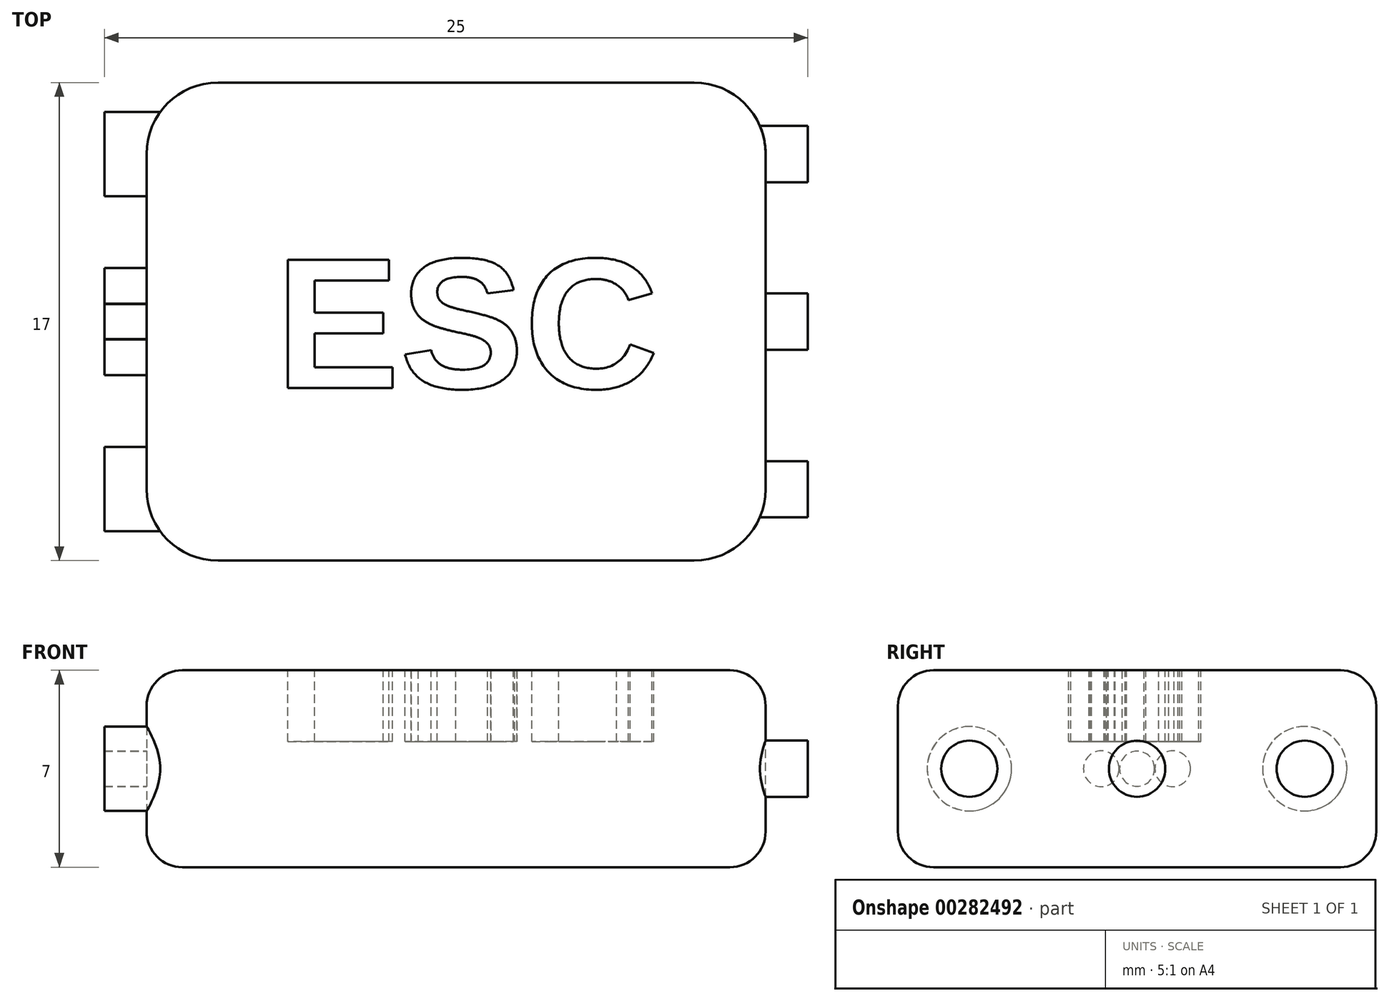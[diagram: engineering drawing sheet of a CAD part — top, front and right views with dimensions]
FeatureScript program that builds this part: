
annotation { "Feature Type Name" : "Feature", "Feature Type Description" : "" }
export const myFeature = defineFeature(function(context is Context, id is Id, definition is map)
    precondition{}
    {
        {
            var Q0;
            Q0=qCreatedBy(makeId("Top.planeOp"),FACE);
            var sketch = newSketch(context, id + "F0", { "sketchPlane" : qUnion([Q0])});
            skLineSegment(sketch, "E0.bottom", {"start": v(0, 0) * mm, "end": v(22, 0) * mm});
            skLineSegment(sketch, "E0.top", {"start": v(0, 17) * mm, "end": v(22, 17) * mm});
            skLineSegment(sketch, "E0.left", {"start": v(0, 0) * mm, "end": v(0, 17) * mm});
            skLineSegment(sketch, "E0.right", {"start": v(22, 0) * mm, "end": v(22, 17) * mm});
            skSolve(sketch);
        }
        {
            var Q0;
            Q0=makeQuery(id+"F0.imprint","IMPRINT",FACE,{"disambiguationData":[TD([[makeQuery(id+"F0.imprint","IMPRINT",EDGE,{"derivedFrom":sQuery(id+"F0.wireOp",EDGE,"E0.bottom")}),1.0]])]});
            extrude(context, id + "F1", {"entities" : qUnion([Q0]), "depth" : 7 * mm});
        }
        {
            var Q0;
            Q0=makeQuery(id+"F1.opExtrude","SWEPT_EDGE",EDGE,{"disambiguationData":[OSD([sQuery(id+"F0.wireOp",EDGE,"E0.bottom"),sQuery(id+"F0.wireOp",EDGE,"E0.left")])]});
            var Q1;
            Q1=makeQuery(id+"F1.opExtrude","SWEPT_EDGE",EDGE,{"disambiguationData":[OSD([sQuery(id+"F0.wireOp",EDGE,"E0.top"),sQuery(id+"F0.wireOp",EDGE,"E0.right")])]});
            var Q2;
            Q2=makeQuery(id+"F1.opExtrude","SWEPT_EDGE",EDGE,{"disambiguationData":[OSD([sQuery(id+"F0.wireOp",EDGE,"E0.bottom"),sQuery(id+"F0.wireOp",EDGE,"E0.right")])]});
            var Q3;
            Q3=makeQuery(id+"F1.opExtrude","SWEPT_EDGE",EDGE,{"disambiguationData":[OSD([sQuery(id+"F0.wireOp",EDGE,"E0.top"),sQuery(id+"F0.wireOp",EDGE,"E0.left")])]});
            fillet(context, id + "F2", {"entities" : qUnion([Q0, Q1, Q2, Q3]), "radius" : 2.54 * mm, "tangentPropagation" : true, "allowEdgeOverflow" : false});
        }
        {
            var Q0;
            Q0=makeQuery(id+"F1.opExtrude","CAP_EDGE",EDGE,{"disambiguationData":[OSD([sQuery(id+"F0.wireOp",EDGE,"E0.top")])],"isStart":false});
            fillet(context, id + "F3", {"entities" : qUnion([Q0]), "radius" : 1.27 * mm, "tangentPropagation" : true, "allowEdgeOverflow" : false});
        }
        {
            var Q0;
            Q0=makeQuery(id+"F1.opExtrude","CAP_FACE",FACE,{"disambiguationData":[OSD([sQuery(id+"F0.wireOp",EDGE,"E0.bottom"),sQuery(id+"F0.wireOp",EDGE,"E0.top"),sQuery(id+"F0.wireOp",EDGE,"E0.left"),sQuery(id+"F0.wireOp",EDGE,"E0.right")])],"isStart":false});
            var sketch = newSketch(context, id + "F4", { "sketchPlane" : qUnion([Q0])});
            skText(sketch, "E1", { "text": "ESC", "fontName": "Arimo-Bold.ttf"});
            const initialGuessF4  = {"E1": [0.00458, 0.00614, 1, 0, 0.00477]};
            skSetInitialGuess(sketch, initialGuessF4);
            skSolve(sketch);
        }
        {
            var Q0;
            Q0 = qSketchRegion(id + "F4", true);
            extrude(context, id + "F5", {"entities" : qUnion([Q0]), "operationType" : NewBodyOperationType.REMOVE, "oppositeDirection" : true, "depth" : 2.54 * mm});
        }
        {
            var Q0;
            Q0=makeQuery(id+"F1.opExtrude","SWEPT_FACE",FACE,{"disambiguationData":[OSD([sQuery(id+"F0.wireOp",EDGE,"E0.left")])]});
            var sketch = newSketch(context, id + "F6", { "sketchPlane" : qUnion([Q0])});
            skCircle(sketch, "E2", {"center": v(-2.54, 3.5) * mm, "radius": 1.5 * mm});
            skCircle(sketch, "E3", {"center": v(-14.46, 3.5) * mm, "radius": 1.5 * mm});
            skSolve(sketch);
        }
        {
            var Q0;
            {var subQ0=sQuery(id+"F6.wireOp",EDGE,"E3");var subQ1=sQuery(id+"F0.wireOp",EDGE,"E0.left");var subQ2=makeQuery(id+"F2.opFillet","BLEND_EDGE",EDGE,{"blendedFrom":[makeQuery(id+"F1.opExtrude","SWEPT_EDGE",EDGE,{"disambiguationData":[OSD([sQuery(id+"F0.wireOp",EDGE,"E0.top"),subQ1])]}),makeQuery(id+"F1.opExtrude","SWEPT_FACE",FACE,{"disambiguationData":[OSD([subQ1])]})],"blendedInto":[makeQuery(id+"F1.opExtrude","SWEPT_FACE",FACE,{"disambiguationData":[OSD([subQ1])]})]});var subQ3=makeQuery(id+"F6.imprint","INTERSECT",VERTEX,{"disambiguationData":[OD(0.0)],"derivedFrom":[subQ2,subQ0]});Q0=makeQuery(id+"F6.imprint","IMPRINT",FACE,{"disambiguationData":[TD([[makeQuery(id+"F6.imprint","IMPRINT",EDGE,{"disambiguationData":[TD([[subQ3,-1.0]])],"derivedFrom":subQ0}),1.0]])]});}
            var Q1;
            {var subQ0=sQuery(id+"F6.wireOp",EDGE,"E3");var subQ1=sQuery(id+"F0.wireOp",EDGE,"E0.left");var subQ2=makeQuery(id+"F2.opFillet","BLEND_EDGE",EDGE,{"blendedFrom":[makeQuery(id+"F1.opExtrude","SWEPT_EDGE",EDGE,{"disambiguationData":[OSD([sQuery(id+"F0.wireOp",EDGE,"E0.top"),subQ1])]}),makeQuery(id+"F1.opExtrude","SWEPT_FACE",FACE,{"disambiguationData":[OSD([subQ1])]})],"blendedInto":[makeQuery(id+"F1.opExtrude","SWEPT_FACE",FACE,{"disambiguationData":[OSD([subQ1])]})]});var subQ3=makeQuery(id+"F6.imprint","INTERSECT",VERTEX,{"disambiguationData":[OD(0.0)],"derivedFrom":[subQ2,subQ0]});Q1=makeQuery(id+"F6.imprint","IMPRINT",FACE,{"disambiguationData":[TD([[makeQuery(id+"F6.imprint","IMPRINT",EDGE,{"disambiguationData":[TD([[subQ3,1.0]])],"derivedFrom":subQ0}),1.0]])]});}
            var Q2;
            {var subQ0=sQuery(id+"F6.wireOp",EDGE,"E2");var subQ1=sQuery(id+"F0.wireOp",EDGE,"E0.left");var subQ2=makeQuery(id+"F2.opFillet","BLEND_EDGE",EDGE,{"blendedFrom":[makeQuery(id+"F1.opExtrude","SWEPT_EDGE",EDGE,{"disambiguationData":[OSD([sQuery(id+"F0.wireOp",EDGE,"E0.bottom"),subQ1])]}),makeQuery(id+"F1.opExtrude","SWEPT_FACE",FACE,{"disambiguationData":[OSD([subQ1])]})],"blendedInto":[makeQuery(id+"F1.opExtrude","SWEPT_FACE",FACE,{"disambiguationData":[OSD([subQ1])]})]});var subQ3=makeQuery(id+"F6.imprint","INTERSECT",VERTEX,{"disambiguationData":[OD(0.0)],"derivedFrom":[subQ2,subQ0]});Q2=makeQuery(id+"F6.imprint","IMPRINT",FACE,{"disambiguationData":[TD([[makeQuery(id+"F6.imprint","IMPRINT",EDGE,{"disambiguationData":[TD([[subQ3,-1.0]])],"derivedFrom":subQ0}),1.0]])]});}
            var Q3;
            {var subQ0=sQuery(id+"F6.wireOp",EDGE,"E2");var subQ1=sQuery(id+"F0.wireOp",EDGE,"E0.left");var subQ2=makeQuery(id+"F2.opFillet","BLEND_EDGE",EDGE,{"blendedFrom":[makeQuery(id+"F1.opExtrude","SWEPT_EDGE",EDGE,{"disambiguationData":[OSD([sQuery(id+"F0.wireOp",EDGE,"E0.bottom"),subQ1])]}),makeQuery(id+"F1.opExtrude","SWEPT_FACE",FACE,{"disambiguationData":[OSD([subQ1])]})],"blendedInto":[makeQuery(id+"F1.opExtrude","SWEPT_FACE",FACE,{"disambiguationData":[OSD([subQ1])]})]});var subQ3=makeQuery(id+"F6.imprint","INTERSECT",VERTEX,{"disambiguationData":[OD(0.0)],"derivedFrom":[subQ2,subQ0]});Q3=makeQuery(id+"F6.imprint","IMPRINT",FACE,{"disambiguationData":[TD([[makeQuery(id+"F6.imprint","IMPRINT",EDGE,{"disambiguationData":[TD([[subQ3,1.0]])],"derivedFrom":subQ0}),1.0]])]});}
            extrude(context, id + "F7", {"entities" : qUnion([Q0, Q1, Q2, Q3]), "operationType" : NewBodyOperationType.ADD, "endBound" : BoundingType.SYMMETRIC, "depth" : 3 * mm});
        }
        {
            var Q0;
            Q0=makeQuery(id+"F1.opExtrude","CAP_FACE",FACE,{"disambiguationData":[OSD([sQuery(id+"F0.wireOp",EDGE,"E0.bottom"),sQuery(id+"F0.wireOp",EDGE,"E0.top"),sQuery(id+"F0.wireOp",EDGE,"E0.left"),sQuery(id+"F0.wireOp",EDGE,"E0.right")])],"isStart":true});
            fillet(context, id + "F8", {"entities" : qUnion([Q0]), "radius" : 1.27 * mm, "tangentPropagation" : true, "allowEdgeOverflow" : false});
        }
        {
            var Q0;
            Q0=makeQuery(id+"F1.opExtrude","SWEPT_FACE",FACE,{"disambiguationData":[OSD([sQuery(id+"F0.wireOp",EDGE,"E0.left")])]});
            var sketch = newSketch(context, id + "F9", { "sketchPlane" : qUnion([Q0])});
            skCircle(sketch, "E4", {"center": v(-9.77, 3.5) * mm, "radius": 0.64 * mm});
            skCircle(sketch, "E5", {"center": v(-8.5, 3.5) * mm, "radius": 0.64 * mm});
            skCircle(sketch, "E6", {"center": v(-7.23, 3.5) * mm, "radius": 0.64 * mm});
            skLineSegment(sketch, "E7", {"start": v(-7.23, 3.5) * mm, "end": v(-9.77, 3.5) * mm, "construction": true});
            skSolve(sketch);
        }
        {
            var Q0;
            Q0=makeQuery(id+"F9.imprint","IMPRINT",FACE,{"disambiguationData":[TD([[makeQuery(id+"F9.imprint","IMPRINT",EDGE,{"derivedFrom":sQuery(id+"F9.wireOp",EDGE,"E4")}),1.0]])]});
            var Q1;
            Q1=makeQuery(id+"F9.imprint","IMPRINT",FACE,{"disambiguationData":[TD([[makeQuery(id+"F9.imprint","IMPRINT",EDGE,{"derivedFrom":sQuery(id+"F9.wireOp",EDGE,"E6")}),1.0]])]});
            extrude(context, id + "F10", {"entities" : qUnion([Q0, Q1]), "operationType" : NewBodyOperationType.ADD, "depth" : 1.5 * mm});
        }
        {
            var Q0;
            Q0=makeQuery(id+"F1.opExtrude","SWEPT_FACE",FACE,{"disambiguationData":[OSD([sQuery(id+"F0.wireOp",EDGE,"E0.left")])]});
            var sketch = newSketch(context, id + "F11", { "sketchPlane" : qUnion([Q0])});
            skCircle(sketch, "E8", {"center": v(-8.5, 3.5) * mm, "radius": 0.62 * mm});
            skCircle(sketch, "E9.0", {"center": v(-7.23, 3.5) * mm, "radius": 0.64 * mm});
            skCircle(sketch, "E10.0", {"center": v(-9.77, 3.5) * mm, "radius": 0.64 * mm});
            skLineSegment(sketch, "E11", {"start": v(-7.23, 3.5) * mm, "end": v(-9.77, 3.5) * mm});
            skSolve(sketch);
        }
        {
            var Q0;
            {var subQ0=sQuery(id+"F11.wireOp",EDGE,"E11");var subQ1=sQuery(id+"F11.wireOp",EDGE,"E8");var subQ2=makeQuery(id+"F11.imprint","INTERSECT",VERTEX,{"derivedFrom":[subQ1,sQuery(id+"F11.wireOp",EDGE,"E9.0"),subQ0]});Q0=makeQuery(id+"F11.imprint","IMPRINT",FACE,{"disambiguationData":[TD([[makeQuery(id+"F11.imprint","IMPRINT",EDGE,{"disambiguationData":[TD([[subQ2,-1.0]])],"derivedFrom":subQ1}),1.0]])]});}
            var Q1;
            {var subQ0=sQuery(id+"F11.wireOp",EDGE,"E11");var subQ1=sQuery(id+"F11.wireOp",EDGE,"E8");var subQ2=makeQuery(id+"F11.imprint","INTERSECT",VERTEX,{"derivedFrom":[subQ1,sQuery(id+"F11.wireOp",EDGE,"E9.0"),subQ0]});Q1=makeQuery(id+"F11.imprint","IMPRINT",FACE,{"disambiguationData":[TD([[makeQuery(id+"F11.imprint","IMPRINT",EDGE,{"disambiguationData":[TD([[subQ2,1.0]])],"derivedFrom":subQ1}),1.0]])]});}
            extrude(context, id + "F12", {"entities" : qUnion([Q0, Q1]), "operationType" : NewBodyOperationType.ADD, "depth" : 1.5 * mm});
        }
        {
            var Q0;
            Q0=makeQuery(id+"F11.imprint","IMPRINT",FACE,{"disambiguationData":[TD([[makeQuery(id+"F11.imprint","IMPRINT",EDGE,{"derivedFrom":sQuery(id+"F11.wireOp",EDGE,"E8")}),1.0]])]});
            extrude(context, id + "F13", {"entities" : qUnion([Q0]), "operationType" : NewBodyOperationType.ADD, "depth" : 1.5 * mm});
        }
        {
            var Q0;
            Q0=makeQuery(id+"F1.opExtrude","SWEPT_FACE",FACE,{"disambiguationData":[OSD([sQuery(id+"F0.wireOp",EDGE,"E0.right")])]});
            var sketch = newSketch(context, id + "F14", { "sketchPlane" : qUnion([Q0])});
            skCircle(sketch, "E12", {"center": v(2.54, 3.5) * mm, "radius": 1 * mm});
            skCircle(sketch, "E13", {"center": v(8.5, 3.5) * mm, "radius": 1 * mm});
            skCircle(sketch, "E14", {"center": v(14.46, 3.5) * mm, "radius": 1 * mm});
            skLineSegment(sketch, "E15", {"start": v(2.54, 3.5) * mm, "end": v(14.46, 3.5) * mm, "construction": true});
            skSolve(sketch);
        }
        {
            var Q0;
            {var subQ0=sQuery(id+"F14.wireOp",EDGE,"E12");var subQ1=sQuery(id+"F0.wireOp",EDGE,"E0.right");var subQ2=makeQuery(id+"F2.opFillet","BLEND_EDGE",EDGE,{"blendedFrom":[makeQuery(id+"F1.opExtrude","SWEPT_EDGE",EDGE,{"disambiguationData":[OSD([sQuery(id+"F0.wireOp",EDGE,"E0.bottom"),subQ1])]}),makeQuery(id+"F1.opExtrude","SWEPT_FACE",FACE,{"disambiguationData":[OSD([subQ1])]})],"blendedInto":[makeQuery(id+"F1.opExtrude","SWEPT_FACE",FACE,{"disambiguationData":[OSD([subQ1])]})]});var subQ3=makeQuery(id+"F14.imprint","INTERSECT",VERTEX,{"disambiguationData":[OD(0.0)],"derivedFrom":[subQ2,subQ0]});Q0=makeQuery(id+"F14.imprint","IMPRINT",FACE,{"disambiguationData":[TD([[makeQuery(id+"F14.imprint","IMPRINT",EDGE,{"disambiguationData":[TD([[subQ3,-1.0]])],"derivedFrom":subQ0}),1.0]])]});}
            var Q1;
            {var subQ0=sQuery(id+"F14.wireOp",EDGE,"E12");var subQ1=sQuery(id+"F0.wireOp",EDGE,"E0.right");var subQ2=makeQuery(id+"F2.opFillet","BLEND_EDGE",EDGE,{"blendedFrom":[makeQuery(id+"F1.opExtrude","SWEPT_EDGE",EDGE,{"disambiguationData":[OSD([sQuery(id+"F0.wireOp",EDGE,"E0.bottom"),subQ1])]}),makeQuery(id+"F1.opExtrude","SWEPT_FACE",FACE,{"disambiguationData":[OSD([subQ1])]})],"blendedInto":[makeQuery(id+"F1.opExtrude","SWEPT_FACE",FACE,{"disambiguationData":[OSD([subQ1])]})]});var subQ3=makeQuery(id+"F14.imprint","INTERSECT",VERTEX,{"disambiguationData":[OD(0.0)],"derivedFrom":[subQ2,subQ0]});Q1=makeQuery(id+"F14.imprint","IMPRINT",FACE,{"disambiguationData":[TD([[makeQuery(id+"F14.imprint","IMPRINT",EDGE,{"disambiguationData":[TD([[subQ3,1.0]])],"derivedFrom":subQ0}),1.0]])]});}
            var Q2;
            Q2=makeQuery(id+"F14.imprint","IMPRINT",FACE,{"disambiguationData":[TD([[makeQuery(id+"F14.imprint","IMPRINT",EDGE,{"derivedFrom":sQuery(id+"F14.wireOp",EDGE,"E13")}),1.0]])]});
            var Q3;
            {var subQ0=sQuery(id+"F14.wireOp",EDGE,"E14");var subQ1=sQuery(id+"F0.wireOp",EDGE,"E0.right");var subQ2=makeQuery(id+"F2.opFillet","BLEND_EDGE",EDGE,{"blendedFrom":[makeQuery(id+"F1.opExtrude","SWEPT_EDGE",EDGE,{"disambiguationData":[OSD([sQuery(id+"F0.wireOp",EDGE,"E0.top"),subQ1])]}),makeQuery(id+"F1.opExtrude","SWEPT_FACE",FACE,{"disambiguationData":[OSD([subQ1])]})],"blendedInto":[makeQuery(id+"F1.opExtrude","SWEPT_FACE",FACE,{"disambiguationData":[OSD([subQ1])]})]});var subQ3=makeQuery(id+"F14.imprint","INTERSECT",VERTEX,{"disambiguationData":[OD(0.0)],"derivedFrom":[subQ2,subQ0]});Q3=makeQuery(id+"F14.imprint","IMPRINT",FACE,{"disambiguationData":[TD([[makeQuery(id+"F14.imprint","IMPRINT",EDGE,{"disambiguationData":[TD([[subQ3,1.0]])],"derivedFrom":subQ0}),1.0]])]});}
            var Q4;
            {var subQ0=sQuery(id+"F14.wireOp",EDGE,"E14");var subQ1=sQuery(id+"F0.wireOp",EDGE,"E0.right");var subQ2=makeQuery(id+"F2.opFillet","BLEND_EDGE",EDGE,{"blendedFrom":[makeQuery(id+"F1.opExtrude","SWEPT_EDGE",EDGE,{"disambiguationData":[OSD([sQuery(id+"F0.wireOp",EDGE,"E0.top"),subQ1])]}),makeQuery(id+"F1.opExtrude","SWEPT_FACE",FACE,{"disambiguationData":[OSD([subQ1])]})],"blendedInto":[makeQuery(id+"F1.opExtrude","SWEPT_FACE",FACE,{"disambiguationData":[OSD([subQ1])]})]});var subQ3=makeQuery(id+"F14.imprint","INTERSECT",VERTEX,{"disambiguationData":[OD(0.0)],"derivedFrom":[subQ2,subQ0]});Q4=makeQuery(id+"F14.imprint","IMPRINT",FACE,{"disambiguationData":[TD([[makeQuery(id+"F14.imprint","IMPRINT",EDGE,{"disambiguationData":[TD([[subQ3,-1.0]])],"derivedFrom":subQ0}),1.0]])]});}
            extrude(context, id + "F15", {"entities" : qUnion([Q0, Q1, Q2, Q3, Q4]), "operationType" : NewBodyOperationType.ADD, "endBound" : BoundingType.SYMMETRIC, "depth" : 3 * mm});
        }
    });
